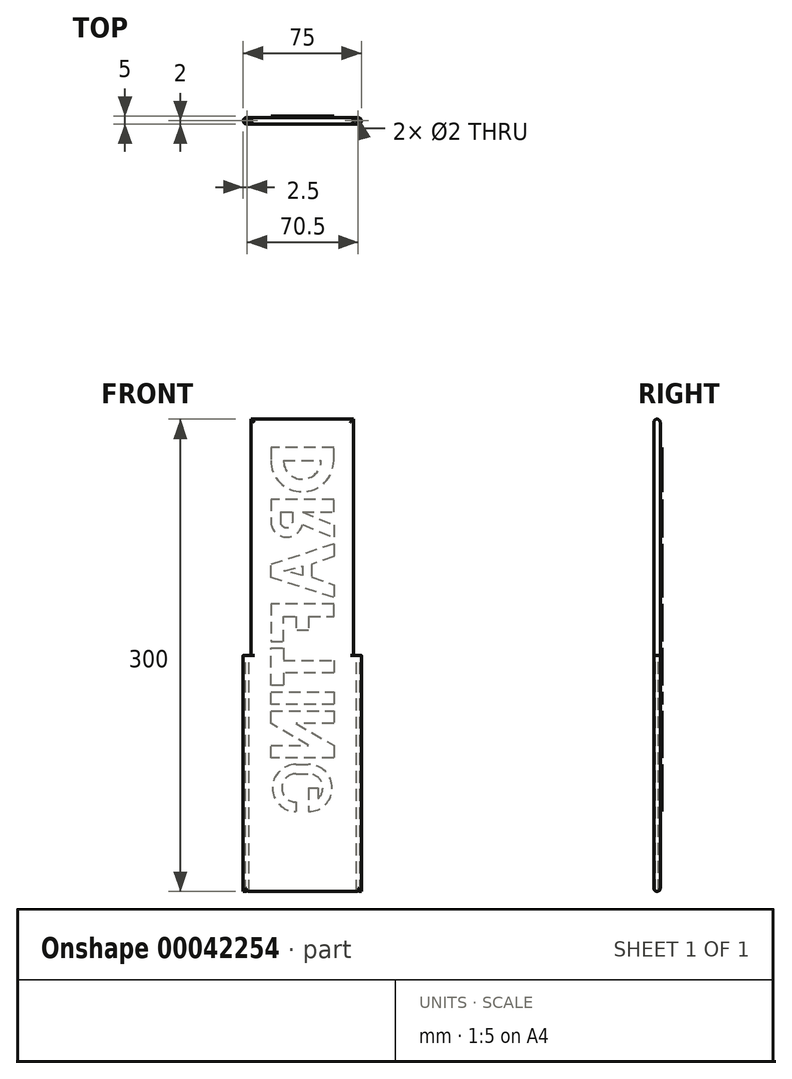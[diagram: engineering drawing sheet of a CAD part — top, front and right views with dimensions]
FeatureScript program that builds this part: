
annotation { "Feature Type Name" : "Feature", "Feature Type Description" : "" }
export const myFeature = defineFeature(function(context is Context, id is Id, definition is map)
    precondition{}
    {
        {
            var Q0;
            Q0=qCreatedBy(makeId("Front.planeOp"),FACE);
            var sketch = newSketch(context, id + "F0", { "sketchPlane" : qUnion([Q0])});
            skLineSegment(sketch, "E0.top", {"start": v(-75, -153.96) * mm, "end": v(0, -153.96) * mm});
            skLineSegment(sketch, "E1", {"start": v(-75, -3.96) * mm, "end": v(-70, -3.96) * mm});
            skLineSegment(sketch, "E2", {"start": v(-70, -3.96) * mm, "end": v(-70, 146.04) * mm});
            skLineSegment(sketch, "E3", {"start": v(0, -3.96) * mm, "end": v(-5, -3.96) * mm});
            skLineSegment(sketch, "E4", {"start": v(-5, -3.96) * mm, "end": v(-5, 146.04) * mm});
            skLineSegment(sketch, "E5", {"start": v(0, -3.96) * mm, "end": v(0, -153.96) * mm});
            skLineSegment(sketch, "E6", {"start": v(-70, 146.04) * mm, "end": v(-5, 146.04) * mm});
            skLineSegment(sketch, "E7", {"start": v(-75, -3.96) * mm, "end": v(-75, -153.96) * mm});
            skSolve(sketch);
        }
        {
            var Q0;
            Q0 = qSketchRegion(id + "F0", true);
            extrude(context, id + "F1", {"entities" : qUnion([Q0]), "depth" : 4 * mm});
        }
        {
            var Q0;
            Q0=makeQuery(id+"F1.opExtrude","SWEPT_FACE",FACE,{"disambiguationData":[OSD([sQuery(id+"F0.wireOp",EDGE,"E1")])]});
            var sketch = newSketch(context, id + "F2", { "sketchPlane" : qUnion([Q0])});
            skLineSegment(sketch, "E8", {"start": v(-70, -4) * mm, "end": v(-75, 0) * mm, "construction": true});
            skCircle(sketch, "E9", {"center": v(-72.5, -2) * mm, "radius": 1 * mm});
            skSolve(sketch);
        }
        {
            var Q0;
            Q0 = qSketchRegion(id + "F2", true);
            extrude(context, id + "F3", {"entities" : qUnion([Q0]), "operationType" : NewBodyOperationType.REMOVE, "oppositeDirection" : true, "depth" : 160.55 * mm});
        }
        {
            var Q0;
            Q0=makeQuery(id+"F1.opExtrude","CAP_EDGE",EDGE,{"disambiguationData":[OSD([sQuery(id+"F0.wireOp",EDGE,"E7")])],"isStart":false});
            var Q1;
            Q1=makeQuery(id+"F1.opExtrude","CAP_EDGE",EDGE,{"disambiguationData":[OSD([sQuery(id+"F0.wireOp",EDGE,"E7")])],"isStart":true});
            var Q2;
            Q2=makeQuery(id+"F1.opExtrude","CAP_EDGE",EDGE,{"disambiguationData":[OSD([sQuery(id+"F0.wireOp",EDGE,"E2")])],"isStart":false});
            var Q3;
            Q3=makeQuery(id+"F1.opExtrude","CAP_EDGE",EDGE,{"disambiguationData":[OSD([sQuery(id+"F0.wireOp",EDGE,"E2")])],"isStart":true});
            var Q4;
            Q4=makeQuery(id+"F1.opExtrude","CAP_EDGE",EDGE,{"disambiguationData":[OSD([sQuery(id+"F0.wireOp",EDGE,"E6")])],"isStart":false});
            var Q5;
            Q5=makeQuery(id+"F1.opExtrude","CAP_EDGE",EDGE,{"disambiguationData":[OSD([sQuery(id+"F0.wireOp",EDGE,"E0.top")])],"isStart":false});
            var Q6;
            Q6=makeQuery(id+"F1.opExtrude","CAP_EDGE",EDGE,{"disambiguationData":[OSD([sQuery(id+"F0.wireOp",EDGE,"E6")])],"isStart":true});
            var Q7;
            Q7=makeQuery(id+"F1.opExtrude","CAP_EDGE",EDGE,{"disambiguationData":[OSD([sQuery(id+"F0.wireOp",EDGE,"E0.top")])],"isStart":true});
            var Q8;
            Q8=makeQuery(id+"F1.opExtrude","CAP_EDGE",EDGE,{"disambiguationData":[OSD([sQuery(id+"F0.wireOp",EDGE,"E4")])],"isStart":true});
            var Q9;
            Q9=makeQuery(id+"F1.opExtrude","CAP_EDGE",EDGE,{"disambiguationData":[OSD([sQuery(id+"F0.wireOp",EDGE,"E4")])],"isStart":false});
            var Q10;
            Q10=makeQuery(id+"F1.opExtrude","CAP_EDGE",EDGE,{"disambiguationData":[OSD([sQuery(id+"F0.wireOp",EDGE,"E5")])],"isStart":true});
            var Q11;
            Q11=makeQuery(id+"F1.opExtrude","CAP_EDGE",EDGE,{"disambiguationData":[OSD([sQuery(id+"F0.wireOp",EDGE,"E5")])],"isStart":false});
            fillet(context, id + "F4", {"entities" : qUnion([Q0, Q1, Q2, Q3, Q4, Q5, Q6, Q7, Q8, Q9, Q10, Q11]), "radius" : 2 * mm, "tangentPropagation" : true, "allowEdgeOverflow" : false});
        }
        {
            var Q0;
            Q0=makeQuery(id+"F1.opExtrude","SWEPT_FACE",FACE,{"disambiguationData":[OSD([sQuery(id+"F0.wireOp",EDGE,"E3")])]});
            var sketch = newSketch(context, id + "F5", { "sketchPlane" : qUnion([Q0])});
            skLineSegment(sketch, "E10", {"start": v(0, -4) * mm, "end": v(-4, -4) * mm, "construction": true});
            skLineSegment(sketch, "E11", {"start": v(-4, -4) * mm, "end": v(0, 0) * mm, "construction": true});
            skCircle(sketch, "E12", {"center": v(-2, -2) * mm, "radius": 1 * mm});
            skSolve(sketch);
        }
        {
            var Q0;
            Q0 = qSketchRegion(id + "F5", true);
            extrude(context, id + "F6", {"entities" : qUnion([Q0]), "operationType" : NewBodyOperationType.REMOVE, "oppositeDirection" : true, "depth" : 158.34 * mm});
        }
        {
            var Q0;
            Q0=makeQuery(id+"F1.opExtrude","CAP_FACE",FACE,{"disambiguationData":[OSD([sQuery(id+"F0.wireOp",EDGE,"E0.top"),sQuery(id+"F0.wireOp",EDGE,"E1"),sQuery(id+"F0.wireOp",EDGE,"E2"),sQuery(id+"F0.wireOp",EDGE,"E3"),sQuery(id+"F0.wireOp",EDGE,"E4"),sQuery(id+"F0.wireOp",EDGE,"E5"),sQuery(id+"F0.wireOp",EDGE,"E6"),sQuery(id+"F0.wireOp",EDGE,"E7")])],"isStart":true});
            var sketch = newSketch(context, id + "F7", { "sketchPlane" : qUnion([Q0])});
            skLineSegment(sketch, "E13", {"start": v(37.5, 144.04) * mm, "end": v(37.5, -151.96) * mm, "construction": true});
            skLineSegment(sketch, "E14", {"start": v(37.5, 144.04) * mm, "end": v(57.5, 144.04) * mm, "construction": true});
            skLineSegment(sketch, "E15", {"start": v(57.5, 144.04) * mm, "end": v(17.5, 144.04) * mm, "construction": true});
            skLineSegment(sketch, "E16", {"start": v(57.5, 144.04) * mm, "end": v(57.5, -151.96) * mm, "construction": true});
            skLineSegment(sketch, "E17", {"start": v(17.5, 144.04) * mm, "end": v(17.5, -151.96) * mm, "construction": true});
            skLineSegment(sketch, "E18", {"start": v(17.5, 127.88) * mm, "end": v(57.5, 127.88) * mm});
            skLineSegment(sketch, "E19", {"start": v(57.5, 127.88) * mm, "end": v(57.5, 119.88) * mm});
            skLineSegment(sketch, "E20", {"start": v(17.5, 119.88) * mm, "end": v(17.5, 127.88) * mm});
            skArc(sketch, "E21", {"start": v(17.5, 119.88) * mm, "mid": v(37.5, 99.88) * mm, "end": v(57.5, 119.88) * mm});
            skLineSegment(sketch, "E22", {"start": v(57.5, 119.88) * mm, "end": v(49.5, 119.88) * mm, "construction": true});
            skLineSegment(sketch, "E23", {"start": v(49.5, 119.88) * mm, "end": v(25.5, 119.88) * mm});
            skLineSegment(sketch, "E24", {"start": v(25.5, 119.88) * mm, "end": v(17.5, 119.88) * mm, "construction": true});
            skArc(sketch, "E25", {"start": v(25.5, 119.88) * mm, "mid": v(37.5, 107.88) * mm, "end": v(49.5, 119.88) * mm});
            skLineSegment(sketch, "E26", {"start": v(17.5, 95.15) * mm, "end": v(57.5, 95.15) * mm});
            skLineSegment(sketch, "E27", {"start": v(57.5, 95.15) * mm, "end": v(57.5, 87.15) * mm});
            skLineSegment(sketch, "E28", {"start": v(57.5, 87.15) * mm, "end": v(37.5, 87.15) * mm, "construction": true});
            skLineSegment(sketch, "E29", {"start": v(17.5, 87.15) * mm, "end": v(17.5, 95.15) * mm});
            skLineSegment(sketch, "E30", {"start": v(17.5, 78.74) * mm, "end": v(17.5, 70.74) * mm});
            skLineSegment(sketch, "E31", {"start": v(57.5, 87.15) * mm, "end": v(57.5, 81.15) * mm});
            skArc(sketch, "E32", {"start": v(37.5, 79.15) * mm, "mid": v(48.4, 71.1) * mm, "end": v(57.5, 81.15) * mm});
            skLineSegment(sketch, "E33", {"start": v(37.5, 79.15) * mm, "end": v(17.5, 70.74) * mm});
            skLineSegment(sketch, "E34", {"start": v(37.5, 87.15) * mm, "end": v(17.5, 78.74) * mm});
            skLineSegment(sketch, "E35", {"start": v(37.5, 87.15) * mm, "end": v(17.5, 87.15) * mm});
            skLineSegment(sketch, "E36", {"start": v(51.5, 87.15) * mm, "end": v(43.5, 87.15) * mm});
            skLineSegment(sketch, "E37", {"start": v(51.5, 87.15) * mm, "end": v(51.5, 81.15) * mm});
            skLineSegment(sketch, "E38", {"start": v(43.5, 81.15) * mm, "end": v(43.5, 87.15) * mm});
            skArc(sketch, "E39", {"start": v(43.5, 81.15) * mm, "mid": v(47.5, 77.15) * mm, "end": v(51.5, 81.15) * mm});
            skLineSegment(sketch, "E40", {"start": v(17.5, 66.74) * mm, "end": v(57.5, 53.61) * mm});
            skLineSegment(sketch, "E41", {"start": v(17.5, 66.74) * mm, "end": v(17.5, 58.74) * mm});
            skLineSegment(sketch, "E42", {"start": v(17.5, 58.74) * mm, "end": v(31.58, 53.7) * mm});
            skLineSegment(sketch, "E43", {"start": v(31.58, 53.7) * mm, "end": v(31.58, 45.7) * mm});
            skLineSegment(sketch, "E44", {"start": v(31.58, 45.7) * mm, "end": v(17.5, 40.78) * mm});
            skLineSegment(sketch, "E45", {"start": v(17.5, 40.78) * mm, "end": v(17.5, 32.78) * mm});
            skLineSegment(sketch, "E46", {"start": v(17.5, 32.78) * mm, "end": v(57.5, 45.61) * mm});
            skLineSegment(sketch, "E47", {"start": v(57.5, 45.61) * mm, "end": v(57.5, 53.61) * mm});
            skLineSegment(sketch, "E48", {"start": v(49.12, 49.7) * mm, "end": v(37.5, 52.7) * mm});
            skLineSegment(sketch, "E49", {"start": v(37.5, 52.7) * mm, "end": v(37.5, 46.7) * mm});
            skLineSegment(sketch, "E50", {"start": v(37.5, 46.7) * mm, "end": v(49.12, 49.7) * mm});
            skLineSegment(sketch, "E51", {"start": v(17.5, 28.78) * mm, "end": v(57.5, 28.78) * mm});
            skLineSegment(sketch, "E52", {"start": v(57.5, 28.78) * mm, "end": v(57.5, 4.78) * mm});
            skLineSegment(sketch, "E53", {"start": v(57.5, 4.78) * mm, "end": v(49.5, 4.78) * mm});
            skLineSegment(sketch, "E54", {"start": v(49.5, 4.78) * mm, "end": v(49.5, 20.78) * mm});
            skLineSegment(sketch, "E55", {"start": v(49.5, 20.78) * mm, "end": v(41.5, 20.78) * mm});
            skLineSegment(sketch, "E56", {"start": v(41.5, 20.78) * mm, "end": v(41.5, 11.78) * mm});
            skLineSegment(sketch, "E57", {"start": v(33.5, 20.78) * mm, "end": v(17.5, 20.78) * mm});
            skLineSegment(sketch, "E58", {"start": v(17.5, 20.78) * mm, "end": v(17.5, 28.78) * mm});
            skLineSegment(sketch, "E59", {"start": v(33.5, 20.78) * mm, "end": v(33.5, 11.78) * mm});
            skLineSegment(sketch, "E60", {"start": v(33.5, 11.78) * mm, "end": v(41.5, 11.78) * mm});
            skLineSegment(sketch, "E61", {"start": v(57.5, 0.78) * mm, "end": v(49.5, 0.78) * mm});
            skLineSegment(sketch, "E62", {"start": v(49.5, 0.78) * mm, "end": v(49.5, -7.22) * mm});
            skLineSegment(sketch, "E63", {"start": v(49.5, -7.22) * mm, "end": v(17.5, -7.22) * mm});
            skLineSegment(sketch, "E64", {"start": v(17.5, -7.22) * mm, "end": v(17.5, -15.22) * mm});
            skLineSegment(sketch, "E65", {"start": v(17.5, -15.22) * mm, "end": v(49.5, -15.22) * mm});
            skLineSegment(sketch, "E66", {"start": v(49.5, -15.22) * mm, "end": v(49.5, -23.22) * mm});
            skLineSegment(sketch, "E67", {"start": v(49.5, -23.22) * mm, "end": v(57.5, -23.22) * mm});
            skLineSegment(sketch, "E68", {"start": v(57.5, -23.22) * mm, "end": v(57.5, 0.78) * mm});
            skLineSegment(sketch, "E69", {"start": v(57.5, -27.22) * mm, "end": v(17.5, -27.22) * mm});
            skLineSegment(sketch, "E70", {"start": v(17.5, -27.22) * mm, "end": v(17.41, -35.22) * mm});
            skLineSegment(sketch, "E71", {"start": v(17.41, -35.22) * mm, "end": v(57.5, -35.22) * mm});
            skLineSegment(sketch, "E72", {"start": v(57.5, -35.22) * mm, "end": v(57.5, -27.22) * mm});
            skLineSegment(sketch, "E73", {"start": v(57.5, -39.22) * mm, "end": v(17.5, -39.22) * mm});
            skLineSegment(sketch, "E74", {"start": v(17.5, -39.22) * mm, "end": v(17.5, -47.22) * mm});
            skLineSegment(sketch, "E75", {"start": v(17.5, -47.22) * mm, "end": v(41.58, -47.22) * mm});
            skLineSegment(sketch, "E76", {"start": v(41.58, -47.22) * mm, "end": v(17.5, -61.22) * mm});
            skLineSegment(sketch, "E77", {"start": v(17.5, -61.22) * mm, "end": v(17.5, -69.22) * mm});
            skLineSegment(sketch, "E78", {"start": v(17.5, -69.22) * mm, "end": v(57.5, -69.22) * mm});
            skLineSegment(sketch, "E79", {"start": v(57.5, -69.22) * mm, "end": v(57.5, -61.22) * mm});
            skLineSegment(sketch, "E80", {"start": v(57.5, -61.22) * mm, "end": v(33.42, -61.22) * mm});
            skLineSegment(sketch, "E81", {"start": v(33.42, -61.22) * mm, "end": v(57.5, -47.22) * mm});
            skLineSegment(sketch, "E82", {"start": v(57.5, -47.22) * mm, "end": v(57.5, -39.22) * mm});
            skLineSegment(sketch, "E83", {"start": v(17.5, -73.22) * mm, "end": v(17.5, -103.22) * mm, "construction": true});
            skLineSegment(sketch, "E84", {"start": v(17.5, -103.22) * mm, "end": v(57.5, -103.22) * mm, "construction": true});
            skLineSegment(sketch, "E85", {"start": v(41.5, -73.22) * mm, "end": v(41.5, -103.22) * mm, "construction": true});
            skLineSegment(sketch, "E86", {"start": v(41.5, -103.22) * mm, "end": v(33.5, -103.22) * mm, "construction": true});
            skLineSegment(sketch, "E87", {"start": v(33.5, -103.22) * mm, "end": v(33.5, -73.22) * mm, "construction": true});
            skArc(sketch, "E88", {"start": v(41.5, -103.22) * mm, "mid": v(56.5, -88.22) * mm, "end": v(41.5, -73.22) * mm});
            skArc(sketch, "E89", {"start": v(33.5, -73.22) * mm, "mid": v(18.5, -88.22) * mm, "end": v(33.5, -103.22) * mm});
            skLineSegment(sketch, "E90", {"start": v(41.5, -73.22) * mm, "end": v(33.5, -73.22) * mm});
            skLineSegment(sketch, "E91", {"start": v(41.5, -73.22) * mm, "end": v(41.5, -79.22) * mm, "construction": true});
            skLineSegment(sketch, "E92", {"start": v(41.5, -79.22) * mm, "end": v(33.5, -79.22) * mm});
            skPoint(sketch, "E93.endSnap0", {"position": v(33.5, -97.22) * mm});
            skArc(sketch, "E94", {"start": v(33.5, -79.22) * mm, "mid": v(24.5, -88.22) * mm, "end": v(33.5, -97.22) * mm});
            skArc(sketch, "E95", {"start": v(41.5, -97.22) * mm, "mid": v(50.5, -88.22) * mm, "end": v(41.5, -79.22) * mm});
            skLineSegment(sketch, "E96", {"start": v(41.5, -97.22) * mm, "end": v(41.5, -103.22) * mm});
            skLineSegment(sketch, "E97", {"start": v(33.5, -97.22) * mm, "end": v(33.5, -103.22) * mm});
            skLineSegment(sketch, "E98", {"start": v(33.5, -97.22) * mm, "end": v(33.5, -88.22) * mm});
            skLineSegment(sketch, "E99", {"start": v(33.5, -88.22) * mm, "end": v(27.5, -88.22) * mm});
            skLineSegment(sketch, "E100", {"start": v(27.5, -88.22) * mm, "end": v(27.5, -94.93) * mm});
            skSolve(sketch);
        }
        {
            var Q0;
            Q0 = qSketchRegion(id + "F7", true);
            extrude(context, id + "F8", {"entities" : qUnion([Q0]), "operationType" : NewBodyOperationType.ADD, "depth" : 1 * mm});
        }
    });
